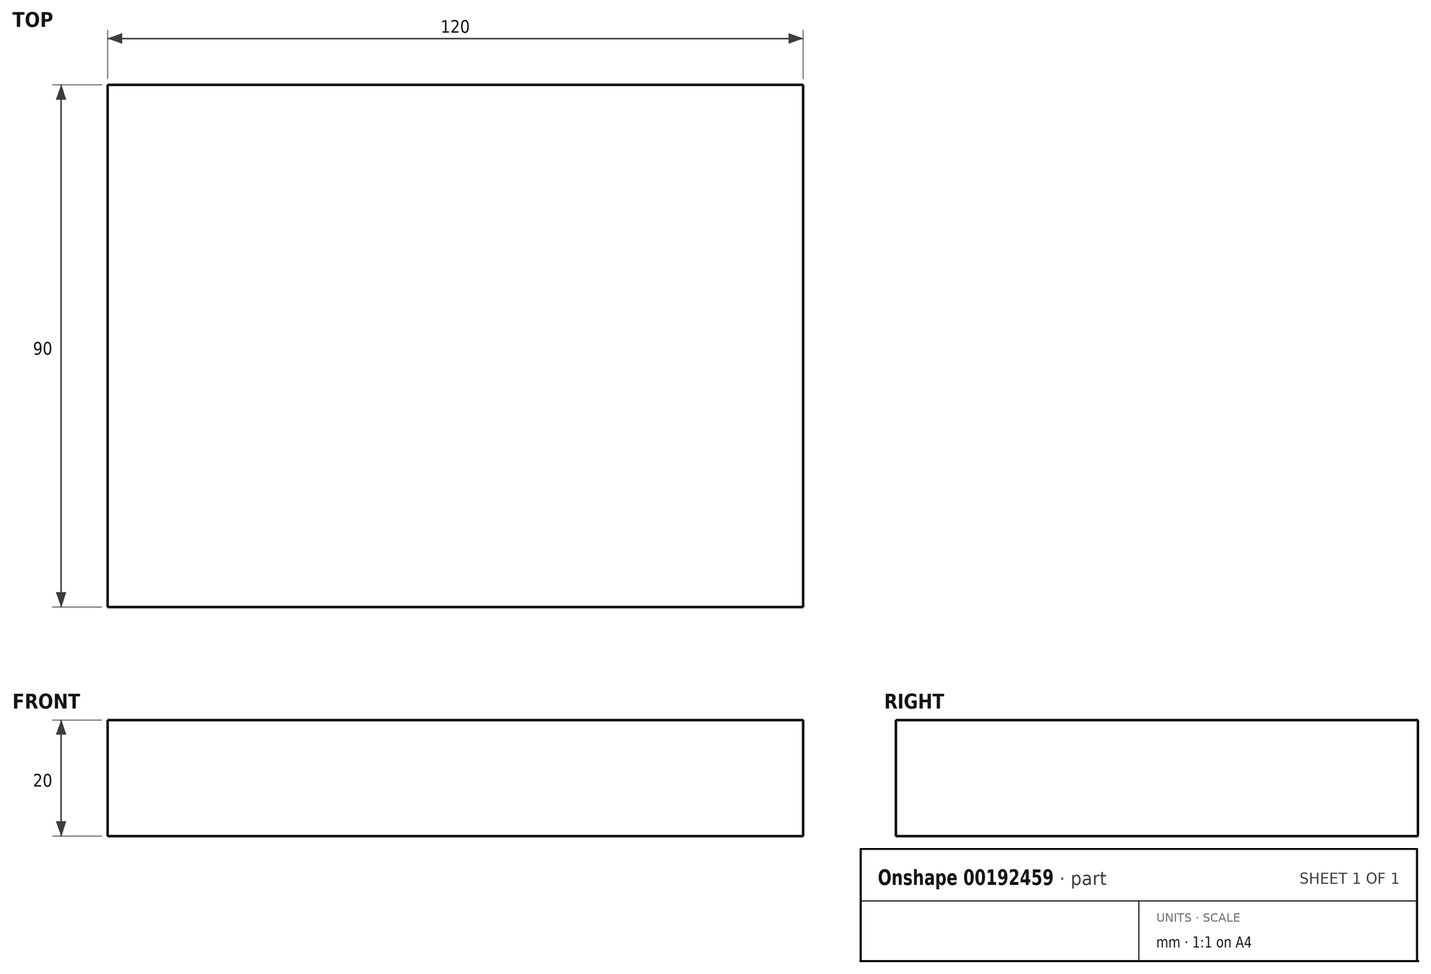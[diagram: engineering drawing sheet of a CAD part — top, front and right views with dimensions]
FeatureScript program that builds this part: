
annotation { "Feature Type Name" : "Feature", "Feature Type Description" : "" }
export const myFeature = defineFeature(function(context is Context, id is Id, definition is map)
    precondition{}
    {
        {
            var Q0;
            Q0=qCreatedBy(makeId("Top.planeOp"),FACE);
            var sketch = newSketch(context, id + "F0", { "sketchPlane" : qUnion([Q0])});
            skLineSegment(sketch, "E0.bottom", {"start": v(60, 45) * mm, "end": v(-60, 45) * mm});
            skLineSegment(sketch, "E0.top", {"start": v(60, -45) * mm, "end": v(-60, -45) * mm});
            skLineSegment(sketch, "E0.left", {"start": v(60, 45) * mm, "end": v(60, -45) * mm});
            skLineSegment(sketch, "E0.right", {"start": v(-60, 45) * mm, "end": v(-60, -45) * mm});
            skPoint(sketch, "E0.middle", {"position": v(0, 0) * mm});
            skSolve(sketch);
        }
        {
            var Q0;
            Q0=makeQuery(id+"F0.imprint","IMPRINT",FACE,{"disambiguationData":[TD([[makeQuery(id+"F0.imprint","IMPRINT",EDGE,{"derivedFrom":sQuery(id+"F0.wireOp",EDGE,"E0.bottom")}),1.0]])]});
            extrude(context, id + "F1", {"entities" : qUnion([Q0]), "depth" : 20 * mm});
        }
    });
